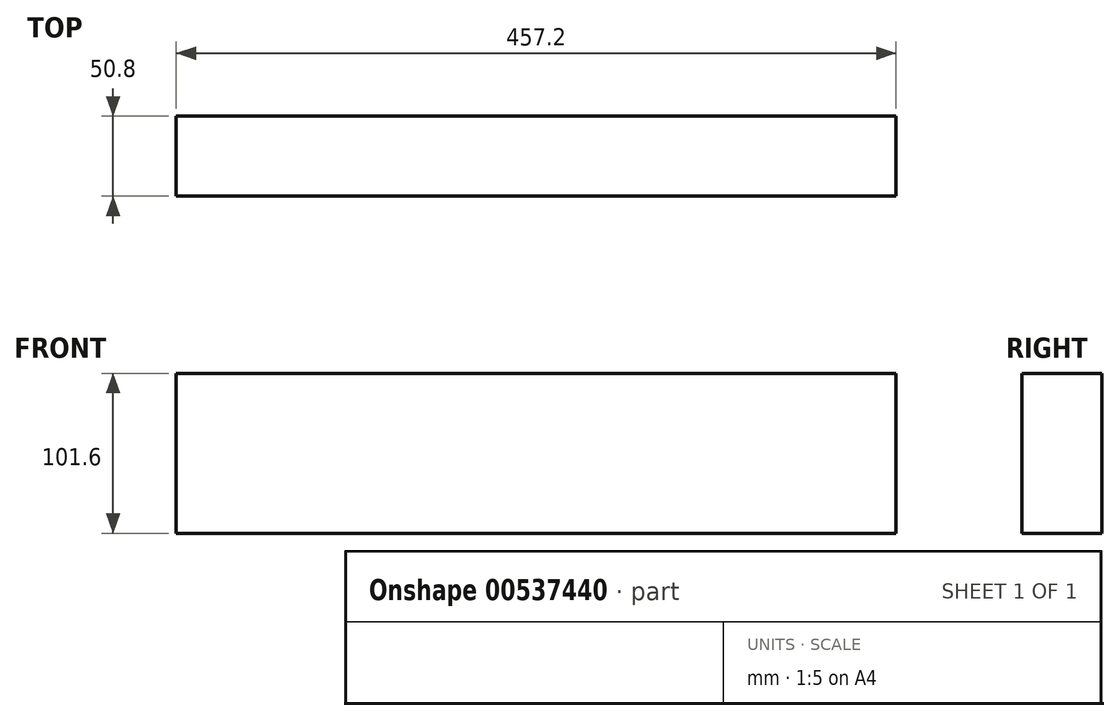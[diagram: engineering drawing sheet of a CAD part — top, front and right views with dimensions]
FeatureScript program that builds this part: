
annotation { "Feature Type Name" : "Feature", "Feature Type Description" : "" }
export const myFeature = defineFeature(function(context is Context, id is Id, definition is map)
    precondition{}
    {
        {
            var Q0;
            Q0=qCreatedBy(makeId("Front.planeOp"),FACE);
            var sketch = newSketch(context, id + "F0", { "sketchPlane" : qUnion([Q0])});
            skLineSegment(sketch, "E0.bottom", {"start": v(228.6, 50.8) * mm, "end": v(-228.6, 50.8) * mm});
            skLineSegment(sketch, "E0.top", {"start": v(228.6, -50.8) * mm, "end": v(-228.6, -50.8) * mm});
            skLineSegment(sketch, "E0.left", {"start": v(228.6, 50.8) * mm, "end": v(228.6, -50.8) * mm});
            skLineSegment(sketch, "E0.right", {"start": v(-228.6, 50.8) * mm, "end": v(-228.6, -50.8) * mm});
            skPoint(sketch, "E0.middle", {"position": v(0, 0) * mm});
            skSolve(sketch);
        }
        {
            var Q0;
            Q0 = qSketchRegion(id + "F0", true);
            extrude(context, id + "F1", {"entities" : qUnion([Q0]), "depth" : 50.8 * mm, "offsetDistance" : 25.4 * mm});
        }
    });
